# Revit family: P300348-009
name_source: partatom
category: Lighting Fixtures
units: mm (PartAtom-declared; Revit-internal decimal feet)

## family parameters
Cut with Voids When Loaded = No
Host = Face
Light Source = No
OmniClass Number = 23.80.70.11.14.17
OmniClass Title = Direct/Indirect
Part Type = Normal
Room Calculation Point = No
Round Connector Dimension = Use Diameter
Shared = Yes

## types (1)
- P300348-143
    Apparent Load = 60 VA
    Assembly Code = D5020200
    Connector Description = Lighting Connector
    Default Elevation = 48 "
    Description = Caisson Collection Four-Light Graphite Clear Glass Urban Industrial Bath Vanity Light
    Features = Ideal for a bathroom
Perfect for urban industrial, farmhouse, and rustic style settings
Gorgeous graphite finish
Bell-shaped clear glass
Mount the light fixture facing up or down
Uses 4 medium base base bulbs that are sold separately (60 W max - LED/CFL/incandescent)
Measures 8-87/100-inch height by 31-87/100-inch length by 7-1/2-inch width (extends from wall)
Certifications: cULus Damp Location Listed
Pairs with the Cirro and Zin collections by Progress Lighting
Our 1-year Limited Warranty guarantees your complete satisfaction with your purchase and includes professional after-sales customer service
    Fixture distribution = Direct
    Glass = Paint - Hubbell - White Texture
    Gold = Hubbell - Gold
    Height = 8.88 "
    Housing Material = Paint - Hubbell - Textured Camera Black
    Lamp = LED/CFL/incandescent
    Length = 31.87 "
    Load Classification = Lighting
    Manufacturer = Progress Lighting
    Model = P300348-143
    Power Factor = 1
    Product Documentation Link = https://hubbellcdn.com
    Product Link = https://www.hubbell.com
    URL = https://www.hubbell.com
    Voltage = 120 V
    Warranty = 1 year Warranty
    Wattage Comments = 60W
    Watts = 60 W
    Wood = Hubbell - Gray

## geometry (parser evidence)
native form markers: Sweep x4
no freeform markers — native parametric forms only
